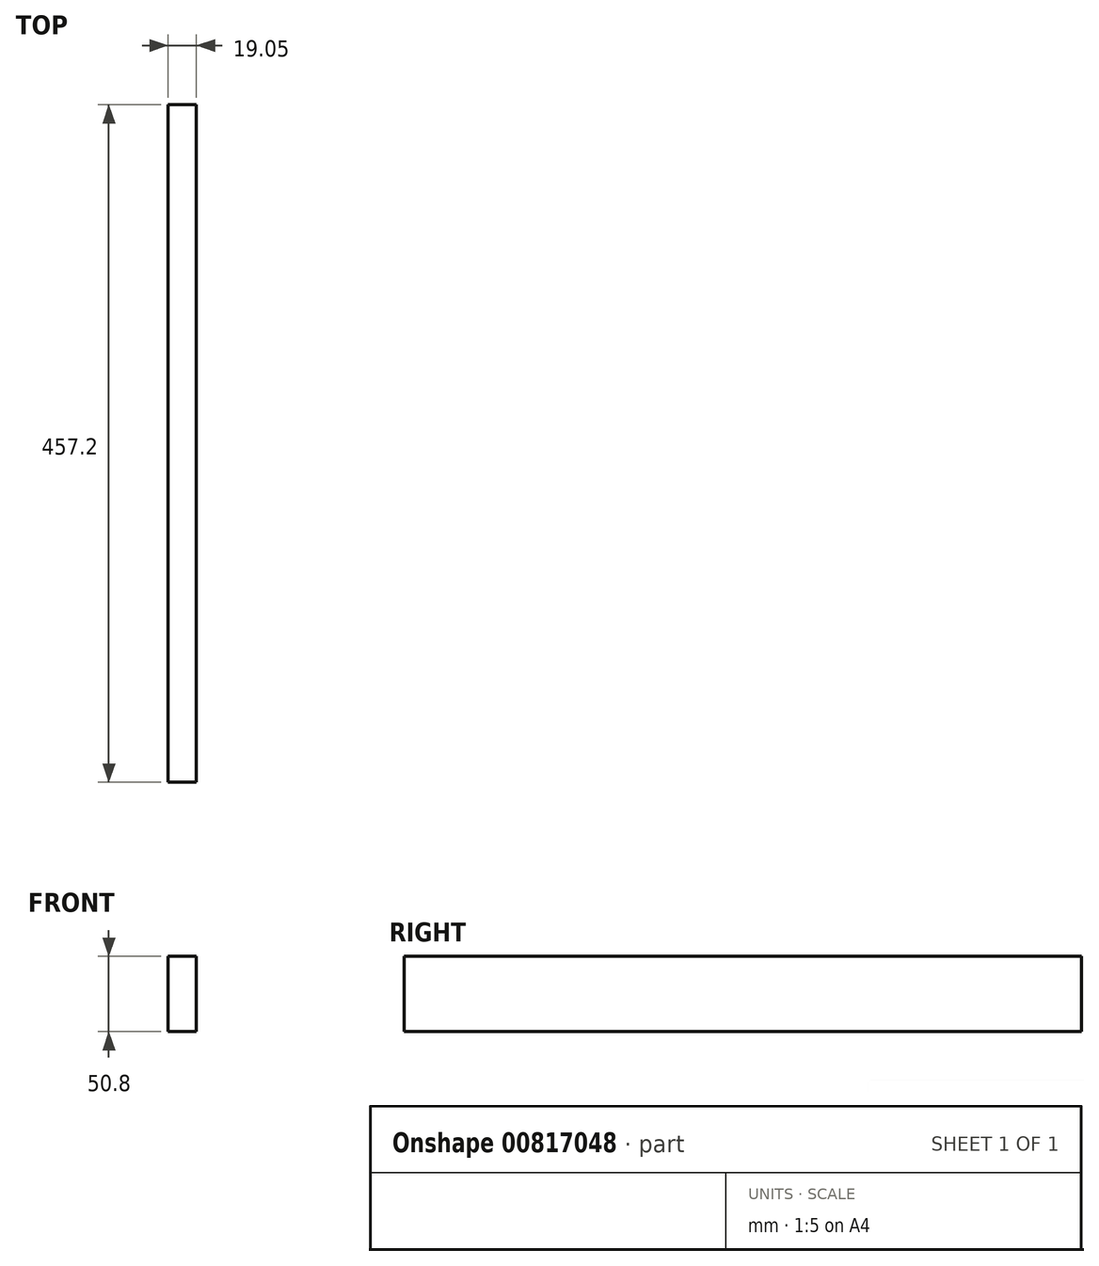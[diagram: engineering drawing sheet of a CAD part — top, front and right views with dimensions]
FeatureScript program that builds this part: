
annotation { "Feature Type Name" : "Feature", "Feature Type Description" : "" }
export const myFeature = defineFeature(function(context is Context, id is Id, definition is map)
    precondition{}
    {
        {
            var Q0;
            Q0=qCreatedBy(makeId("Front.planeOp"),FACE);
            var sketch = newSketch(context, id + "F0", { "sketchPlane" : qUnion([Q0])});
            skLineSegment(sketch, "E0.bottom", {"start": v(0, 0) * mm, "end": v(19.05, 0) * mm});
            skLineSegment(sketch, "E0.top", {"start": v(0, 50.8) * mm, "end": v(19.05, 50.8) * mm});
            skLineSegment(sketch, "E0.left", {"start": v(0, 0) * mm, "end": v(0, 50.8) * mm});
            skLineSegment(sketch, "E0.right", {"start": v(19.05, 0) * mm, "end": v(19.05, 50.8) * mm});
            skSolve(sketch);
        }
        {
            var Q0;
            Q0 = qSketchRegion(id + "F0", true);
            extrude(context, id + "F1", {"entities" : qUnion([Q0]), "depth" : 457.2 * mm, "offsetDistance" : 25.4 * mm});
        }
    });
